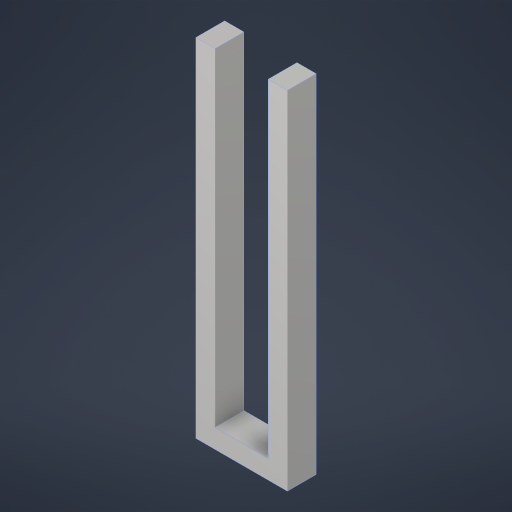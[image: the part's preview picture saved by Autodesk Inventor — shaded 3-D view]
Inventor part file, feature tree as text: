
AUTODESK INVENTOR PART (.ipt)
format: ipt  version: 2024.2 (Build 282272000, 272)  size: 176,640 bytes
history: native  units: in
note: dims shown in document units (in); Inventor stores cm internally (conversion verified against a paired STEP export)
features: extrude x2, sketch x2, projected_geometry x1
ambient origin geometry x8: Origin, YZ Plane, XZ Plane, XY Plane, X Axis, Y Axis, Z Axis, Center Point
bodies: Solid1 (feature_tree)
feature tree (5):
  extrude  "Extrusion1"  Depth=36.0in
  extrude  "Extrusion2"  Depth=2.0in
  sketch  "Sketch1"  dims[d0=9.5in d1=36.0in]
  sketch  "Sketch2"  dims[d2=3.0in d3=0.0in d4=2.0in d5=2.0in d6=2.0in d7=1.0in d8=0.0in]
  projected_geometry  "Project Cut Edges1"
